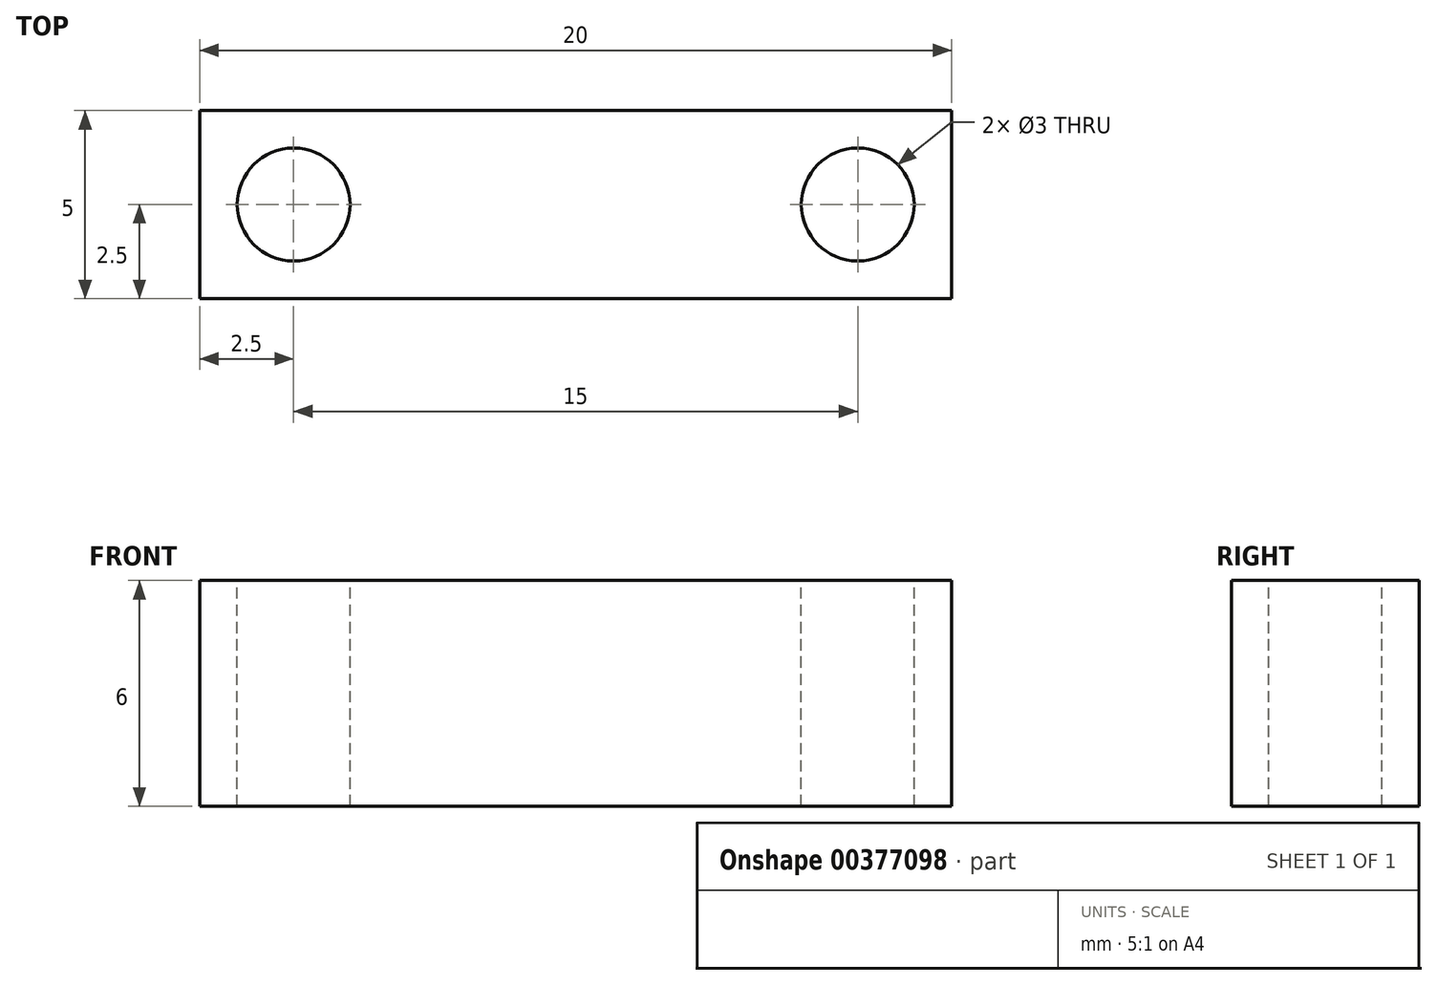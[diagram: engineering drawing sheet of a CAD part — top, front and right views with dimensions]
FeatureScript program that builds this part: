
annotation { "Feature Type Name" : "Feature", "Feature Type Description" : "" }
export const myFeature = defineFeature(function(context is Context, id is Id, definition is map)
    precondition{}
    {
        {
            var Q0;
            Q0=qCreatedBy(makeId("Top.planeOp"),FACE);
            var sketch = newSketch(context, id + "F0", { "sketchPlane" : qUnion([Q0])});
            skLineSegment(sketch, "E0.bottom", {"start": v(-10, 2.5) * mm, "end": v(10, 2.5) * mm});
            skLineSegment(sketch, "E0.top", {"start": v(-10, -2.5) * mm, "end": v(10, -2.5) * mm});
            skLineSegment(sketch, "E0.left", {"start": v(-10, 2.5) * mm, "end": v(-10, -2.5) * mm});
            skLineSegment(sketch, "E0.right", {"start": v(10, 2.5) * mm, "end": v(10, -2.5) * mm});
            skPoint(sketch, "E0.middle", {"position": v(0, 0) * mm});
            skLineSegment(sketch, "E1", {"start": v(0, 0) * mm, "end": v(-7.5, 0) * mm, "construction": true});
            skLineSegment(sketch, "E2.MirrorCS", {"start": v(0, 0) * mm, "end": v(7.5, 0) * mm, "construction": true});
            skCircle(sketch, "E3", {"center": v(-7.5, 0) * mm, "radius": 1.5 * mm});
            skCircle(sketch, "E4.MirrorC", {"center": v(7.5, 0) * mm, "radius": 1.5 * mm});
            skSolve(sketch);
        }
        {
            var Q0;
            Q0=makeQuery(id+"F0.imprint","IMPRINT",FACE,{"disambiguationData":[TD([[makeQuery(id+"F0.imprint","IMPRINT",EDGE,{"derivedFrom":sQuery(id+"F0.wireOp",EDGE,"E0.bottom")}),-1.0]])]});
            extrude(context, id + "F1", {"entities" : qUnion([Q0]), "oppositeDirection" : true, "depth" : 6 * mm});
        }
    });
